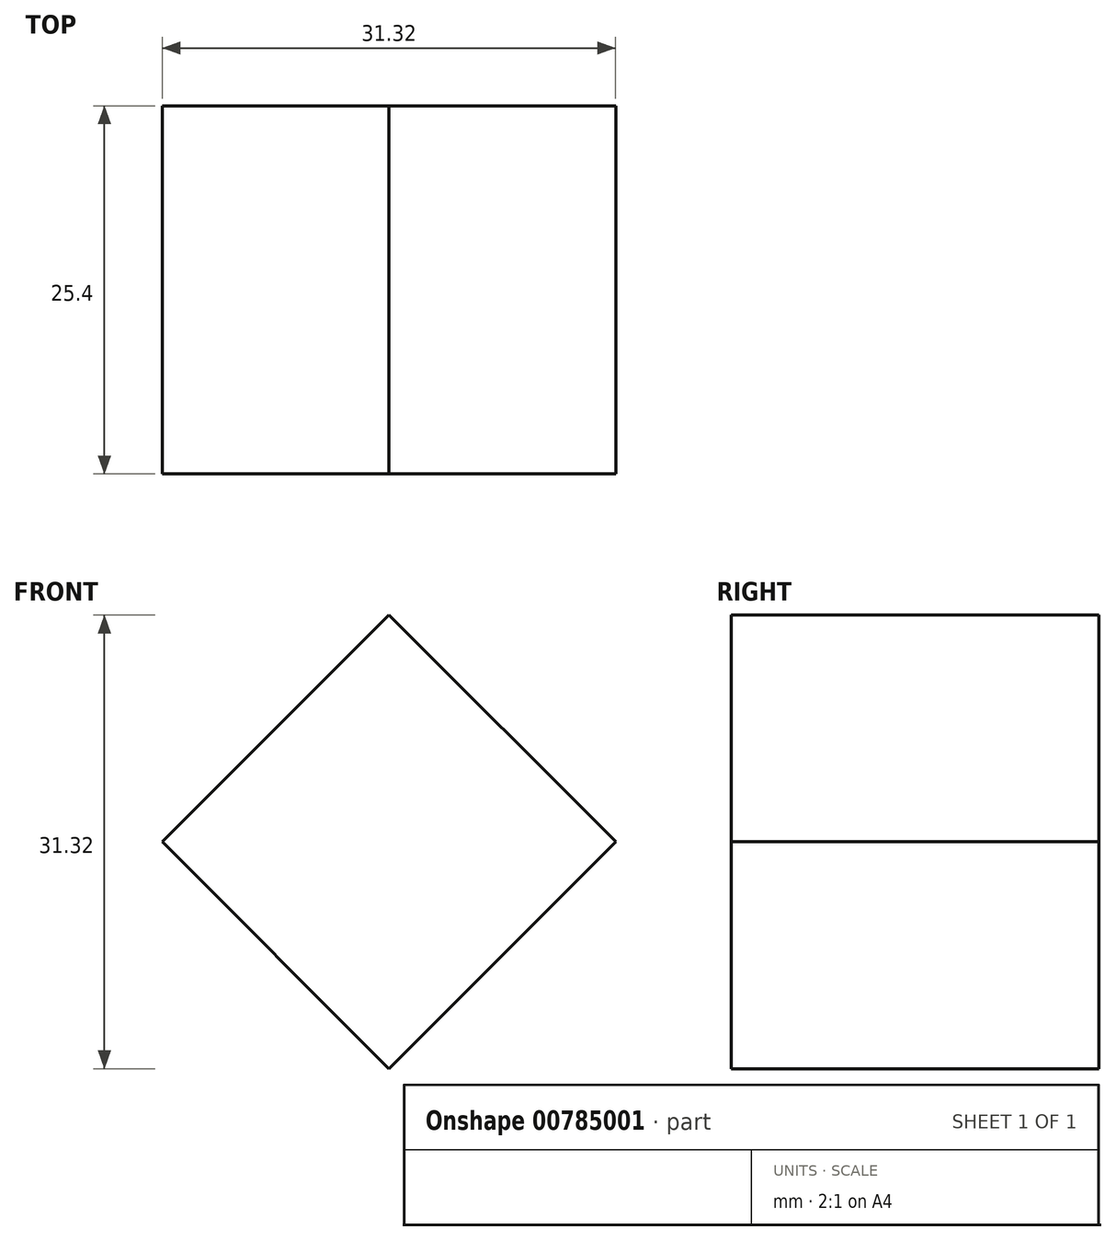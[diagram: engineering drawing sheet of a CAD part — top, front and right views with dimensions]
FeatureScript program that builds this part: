
annotation { "Feature Type Name" : "Feature", "Feature Type Description" : "" }
export const myFeature = defineFeature(function(context is Context, id is Id, definition is map)
    precondition{}
    {
        {
            var Q0;
            Q0=qCreatedBy(makeId("Front.planeOp"),FACE);
            var sketch = newSketch(context, id + "F0", { "sketchPlane" : qUnion([Q0])});
            skLineSegment(sketch, "E0", {"start": v(0, 0) * mm, "end": v(-15.66, 15.66) * mm});
            skLineSegment(sketch, "E1", {"start": v(-15.66, 15.66) * mm, "end": v(0, 31.32) * mm});
            skLineSegment(sketch, "E2", {"start": v(0, 31.32) * mm, "end": v(15.66, 15.66) * mm});
            skLineSegment(sketch, "E3", {"start": v(15.66, 15.66) * mm, "end": v(0, 0) * mm});
            skSolve(sketch);
        }
        {
            var Q0;
            Q0=makeQuery(id+"F0.imprint","IMPRINT",FACE,{"disambiguationData":[TD([[makeQuery(id+"F0.imprint","IMPRINT",EDGE,{"derivedFrom":sQuery(id+"F0.wireOp",EDGE,"E0")}),-1.0]])]});
            extrude(context, id + "F1", {"entities" : qUnion([Q0]), "depth" : 25.4 * mm, "offsetDistance" : 25.4 * mm});
        }
    });
